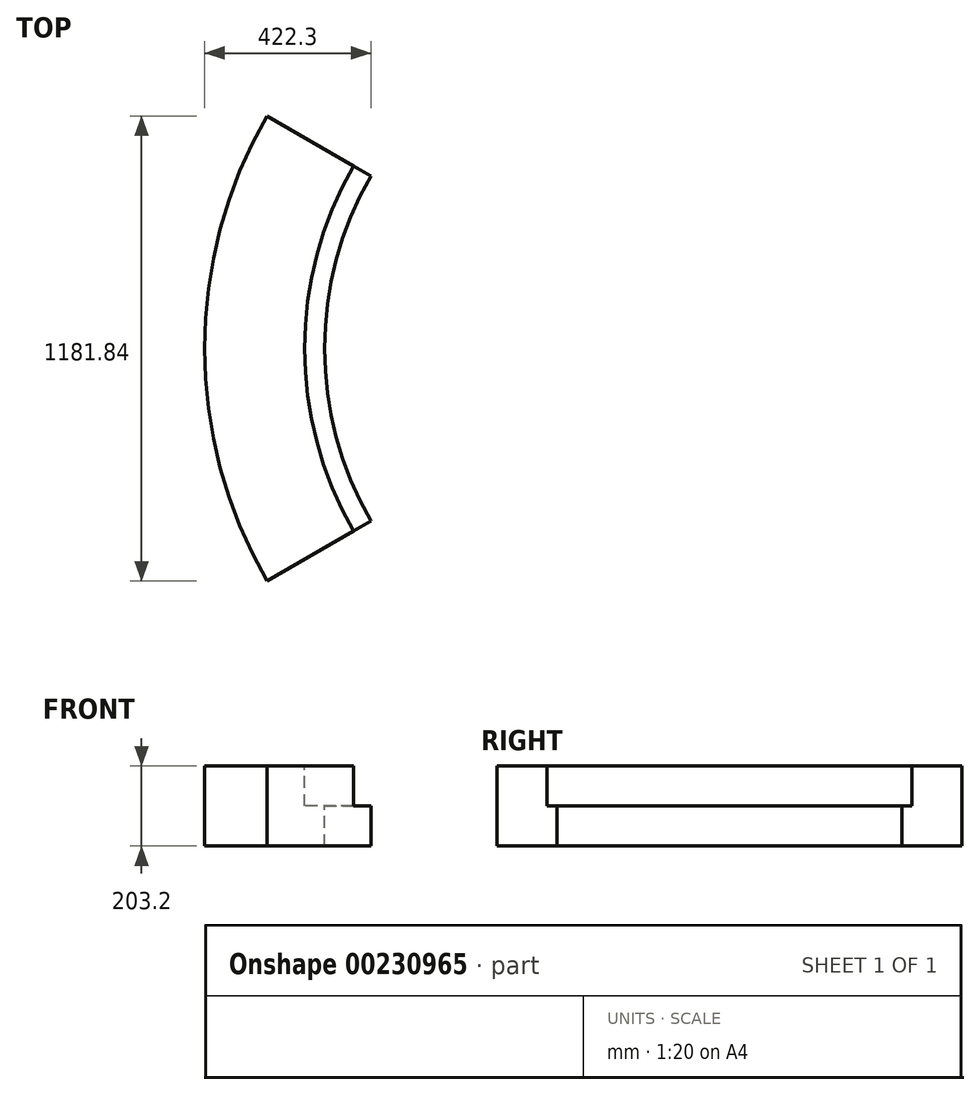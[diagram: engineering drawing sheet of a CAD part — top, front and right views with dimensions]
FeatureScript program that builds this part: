
annotation { "Feature Type Name" : "Feature", "Feature Type Description" : "" }
export const myFeature = defineFeature(function(context is Context, id is Id, definition is map)
    precondition{}
    {
        {
            var Q0;
            Q0=qCreatedBy(makeId("Front.planeOp"),FACE);
            var sketch = newSketch(context, id + "F0", { "sketchPlane" : qUnion([Q0])});
            skLineSegment(sketch, "E0", {"start": v(-1181.84, -1150.9) * mm, "end": v(-927.84, -1150.9) * mm});
            skFitSpline(sketch, "E1", {"points": [v(0, 1953.34) * mm, v(-1100.72, 1005.82) * mm, v(-1321.31, -446.03) * mm, v(-1216.83, -971.67) * mm, v(-1181.84, -1150.9) * mm], "startDerivative": vector(-4000.43, 5.06) * mm, "endDerivative": vector(0, -1489.55) * mm});
            skLineSegment(sketch, "E2", {"start": v(-1099.69, 1008.1) * mm, "end": v(-930.94, 1008.1) * mm});
            skLineSegment(sketch, "E3", {"start": v(-1181.84, -1150.9) * mm, "end": v(-1181.84, -1354.1) * mm});
            skLineSegment(sketch, "E4", {"start": v(-1181.84, -1354.1) * mm, "end": v(-877.04, -1354.1) * mm});
            skLineSegment(sketch, "E5", {"start": v(-877.04, -1354.1) * mm, "end": v(-877.04, -1252.5) * mm});
            skLineSegment(sketch, "E6", {"start": v(-877.04, -1252.5) * mm, "end": v(-927.84, -1252.5) * mm});
            skLineSegment(sketch, "E7", {"start": v(-927.84, -1252.5) * mm, "end": v(-927.84, -1150.9) * mm});
            skFitSpline(sketch, "E8.trimOffspring", {"points": [v(0, -1757.92) * mm, v(-927.84, -1150.9) * mm, v(-1179.31, -127.8) * mm, v(-917.89, 1034.08) * mm, v(0, 1800.66) * mm], "startDerivative": vector(-4973.2, 113.59) * mm, "endDerivative": vector(4756.7, 336.76) * mm});
            skLineSegment(sketch, "E9", {"start": v(-1023.33, 1160.5) * mm, "end": v(-848.12, 1160.5) * mm});
            skLineSegment(sketch, "E10", {"start": v(0, 1953.34) * mm, "end": v(0, 1800.66) * mm});
            skSolve(sketch);
        }
        {
            var Q0;
            Q0=makeQuery(id+"F0.imprint","IMPRINT",FACE,{"disambiguationData":[TD([[makeQuery(id+"F0.imprint","IMPRINT",EDGE,{"derivedFrom":sQuery(id+"F0.wireOp",EDGE,"E0")}),-1.0]])]});
            var Q1;
            Q1=sQuery(id+"F0.wireOp",EDGE,"E10");
            revolve(context, id + "F1", {"entities" : qUnion([Q0]), "axis" : qUnion([Q1]), "revolveType" : RevolveType.SYMMETRIC, "angle" : 60 * degree});
        }
    });
